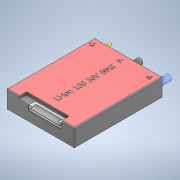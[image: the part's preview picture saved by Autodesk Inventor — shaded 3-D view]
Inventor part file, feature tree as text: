
AUTODESK INVENTOR PART (.ipt)
format: ipt  version: 2020.1 (Build 241239000, 239)  size: 696,832 bytes
history: native  units: mm
features: sketch x5, emboss x2, other x1
ambient origin geometry x8: Origin, YZ Plane, XZ Plane, XY Plane, X Axis, Y Axis, Z Axis, Center Point
bodies: Solid1 (feature_tree)
feature tree (8):
  emboss  "Emboss1"
  emboss  "Emboss2"
  sketch  "Sketch2"  dims[d2=0.05mm d3=0.0mm]
  sketch  "Sketch4"
  sketch  "Sketch5"
  sketch  "Sketch1"  dims[d0=0.05mm d1=0.0mm]
  sketch  "Sketch3"
  other  "Boss-Extrude6"
